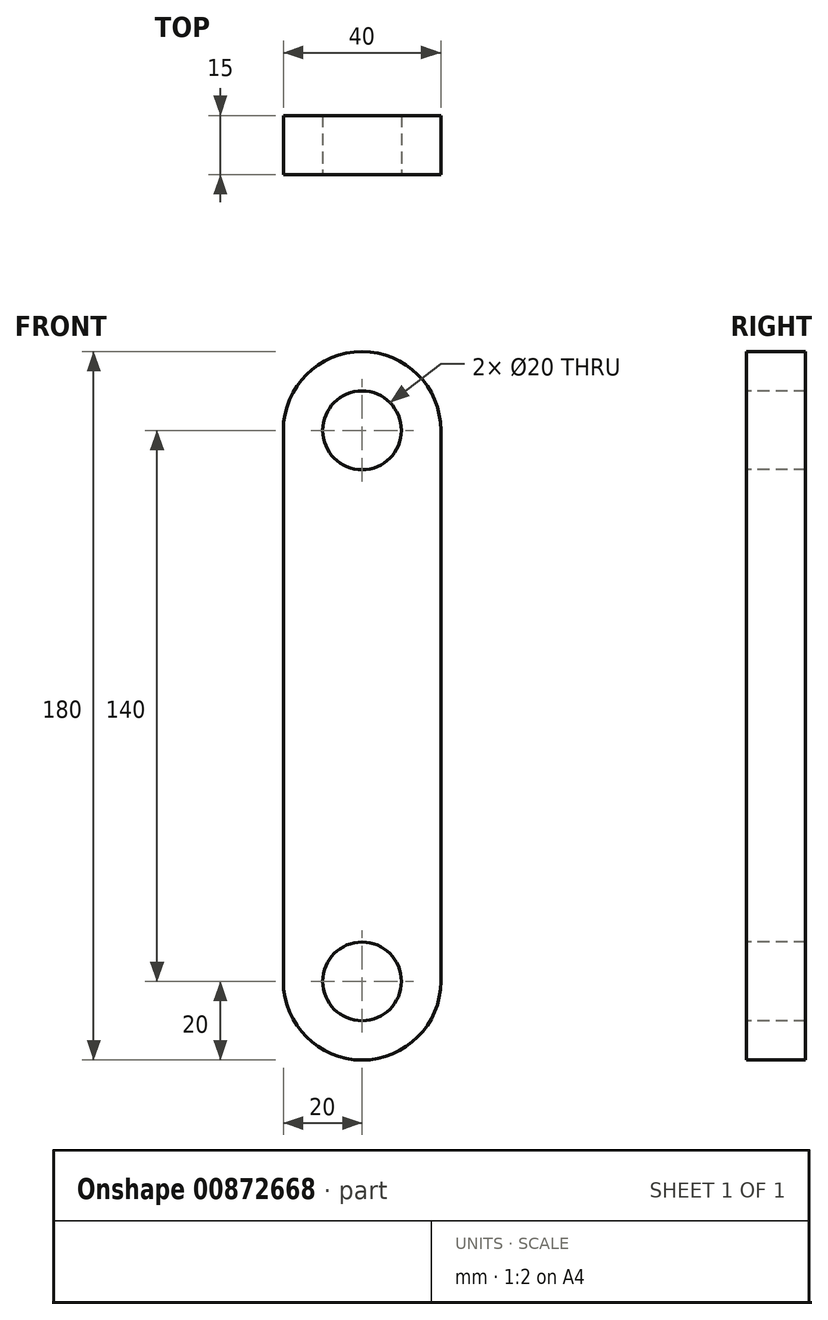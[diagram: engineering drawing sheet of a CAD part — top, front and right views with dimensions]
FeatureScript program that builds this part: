
annotation { "Feature Type Name" : "Feature", "Feature Type Description" : "" }
export const myFeature = defineFeature(function(context is Context, id is Id, definition is map)
    precondition{}
    {
        {
            var Q0;
            Q0=qCreatedBy(makeId("Front.planeOp"),FACE);
            var sketch = newSketch(context, id + "F0", { "sketchPlane" : qUnion([Q0])});
            skCircle(sketch, "E0", {"center": v(0, 0) * mm, "radius": 20 * mm});
            skCircle(sketch, "E1", {"center": v(0, 140) * mm, "radius": 20 * mm});
            skLineSegment(sketch, "E2", {"start": v(-20, 140) * mm, "end": v(-20, 0) * mm});
            skLineSegment(sketch, "E3", {"start": v(20, 140) * mm, "end": v(20, 0) * mm});
            skSolve(sketch);
        }
        {
            var Q0;
            Q0 = qSketchRegion(id + "F0", true);
            extrude(context, id + "F1", {"entities" : qUnion([Q0]), "depth" : 15 * mm, "offsetDistance" : 25 * mm});
        }
        {
            var Q0;
            Q0=makeQuery(id+"F1.opExtrude","CAP_FACE",FACE,{"disambiguationData":[OSD([sQuery(id+"F0.wireOp",EDGE,"E0"),sQuery(id+"F0.wireOp",EDGE,"E1"),sQuery(id+"F0.wireOp",EDGE,"E2"),sQuery(id+"F0.wireOp",EDGE,"E3")])],"isStart":false});
            var sketch = newSketch(context, id + "F2", { "sketchPlane" : qUnion([Q0])});
            skCircle(sketch, "E4", {"center": v(0, 0) * mm, "radius": 10 * mm});
            skCircle(sketch, "E5", {"center": v(0, 140) * mm, "radius": 10 * mm});
            skSolve(sketch);
        }
        {
            var Q0;
            Q0=makeQuery(id+"F2.imprint","IMPRINT",FACE,{"disambiguationData":[TD([[makeQuery(id+"F2.imprint","IMPRINT",EDGE,{"derivedFrom":sQuery(id+"F2.wireOp",EDGE,"E5")}),1.0]])]});
            var Q1;
            Q1=makeQuery(id+"F2.imprint","IMPRINT",FACE,{"disambiguationData":[TD([[makeQuery(id+"F2.imprint","IMPRINT",EDGE,{"derivedFrom":sQuery(id+"F2.wireOp",EDGE,"E4")}),1.0]])]});
            extrude(context, id + "F3", {"entities" : qUnion([Q0, Q1]), "operationType" : NewBodyOperationType.REMOVE, "oppositeDirection" : true, "depth" : 25 * mm, "offsetDistance" : 25 * mm});
        }
    });
